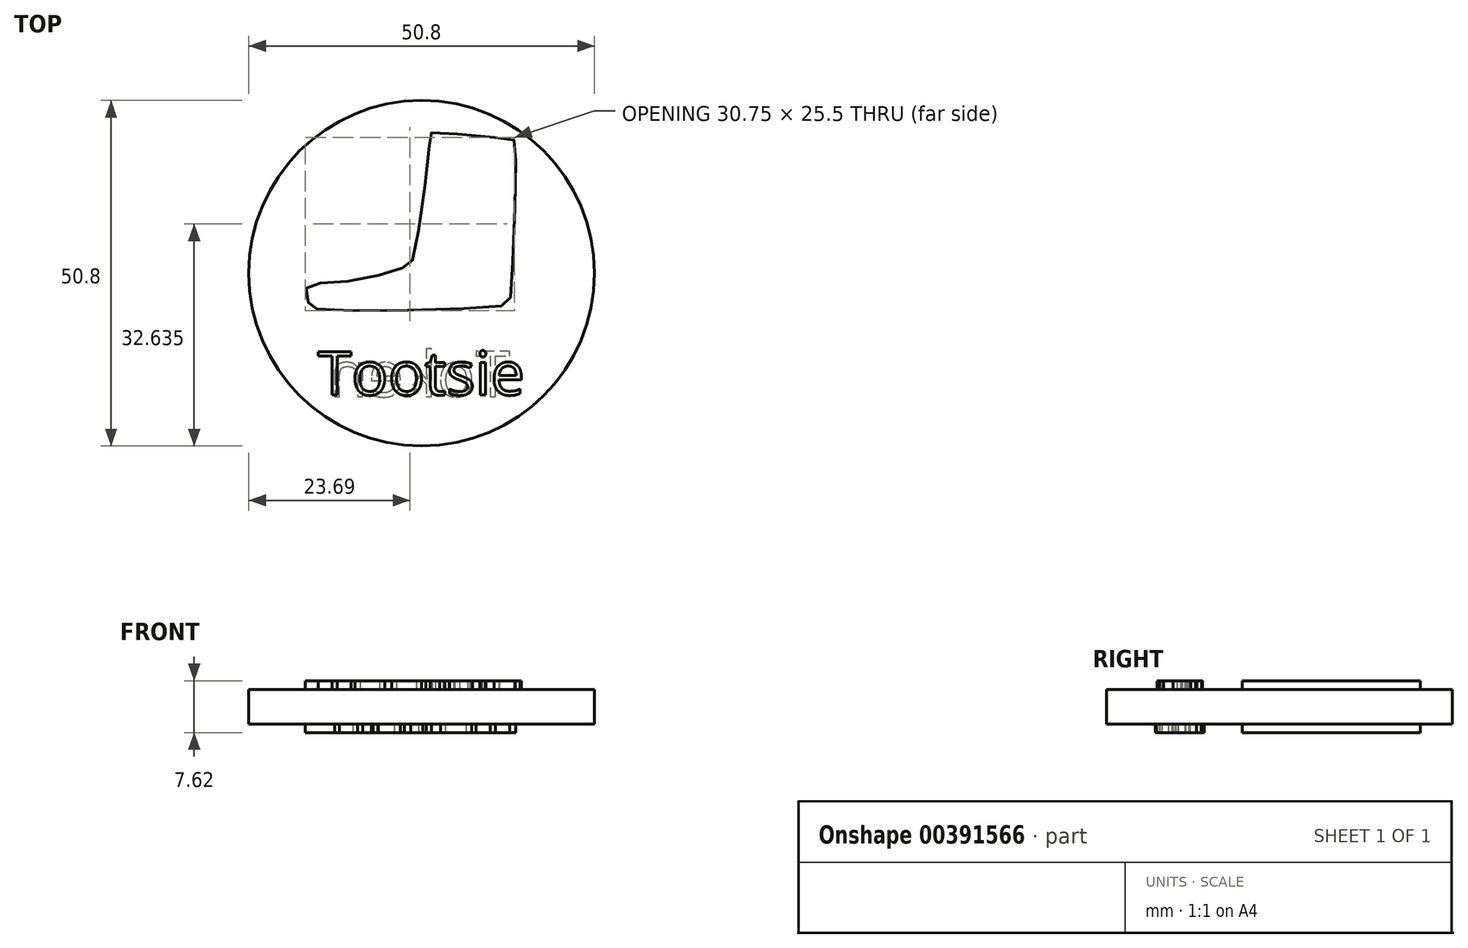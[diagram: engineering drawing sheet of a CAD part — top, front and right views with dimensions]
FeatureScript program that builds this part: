
annotation { "Feature Type Name" : "Feature", "Feature Type Description" : "" }
export const myFeature = defineFeature(function(context is Context, id is Id, definition is map)
    precondition{}
    {
        {
            var Q0;
            Q0=qCreatedBy(makeId("Top.planeOp"),FACE);
            var sketch = newSketch(context, id + "F0", { "sketchPlane" : qUnion([Q0])});
            skCircle(sketch, "E0", {"center": v(0, 0) * mm, "radius": 25.4 * mm});
            skText(sketch, "E1", { "text": "Tootsie", "fontName": "OpenSans-Regular.ttf"});
            skFitSpline(sketch, "E2", {"points": [v(11.72, -4.8) * mm, v(-15.1, -5.31) * mm, v(-16.6, -4.47) * mm, v(-16.95, -2.1) * mm, v(-11.72, -1.26) * mm, v(-2.52, 0.88) * mm, v(-1.16, 2.48) * mm, v(1.2, 20.03) * mm, v(1.54, 20.68) * mm, v(12.92, 19.73) * mm, v(13.72, 19.12) * mm, v(13.07, -3.28) * mm, v(11.72, -4.8) * mm]});
            const initialGuessF0  = {"E1": [-0.01524, -0.0179, 1, 0, 0.00642]};
            skSetInitialGuess(sketch, initialGuessF0);
            skSolve(sketch);
        }
        {
            var Q0;
            Q0=qCreatedBy(makeId("Top.planeOp"),FACE);
            var sketch = newSketch(context, id + "F1", { "sketchPlane" : qUnion([Q0])});
            skCircle(sketch, "E3", {"center": v(0, 0) * mm, "radius": 25.4 * mm});
            skSolve(sketch);
        }
        {
            var Q0;
            Q0 = qSketchRegion(id + "F1", true);
            var Q1;
            Q1 = qSketchRegion(id + "F0", true);
            extrude(context, id + "F2", {"entities" : qUnion([Q0, Q1]), "oppositeDirection" : true, "depth" : 5.08 * mm});
        }
        {
            var Q0;
            Q0=makeQuery(id+"F0.imprint","IMPRINT",FACE,{"disambiguationData":[TD([[makeQuery(id+"F0.imprint","IMPRINT",EDGE,{"derivedFrom":sQuery(id+"F0.wireOp",EDGE,"E2")}),-1.0]])]});
            extrude(context, id + "F3", {"entities" : qUnion([Q0]), "operationType" : NewBodyOperationType.ADD, "depth" : 1.27 * mm, "hasSecondDirection" : true, "secondDirectionOppositeDirection" : true, "secondDirectionDepth" : 6.35 * mm});
        }
        {
            var Q0;
            Q0=makeQuery(id+"F3.boolean.opBoolean","MERGE",FACE,{"derivedFrom":[makeQuery(id+"F2.opExtrude","CAP_FACE",FACE,{"disambiguationData":[OSD([sQuery(id+"F0.wireOp",EDGE,"E0"),sQuery(id+"F0.wireOp",EDGE,"E1.sketch_text.stroke-0"),sQuery(id+"F0.wireOp",EDGE,"E1.sketch_text.stroke-1"),sQuery(id+"F0.wireOp",EDGE,"E1.sketch_text.stroke-2"),sQuery(id+"F0.wireOp",EDGE,"E1.sketch_text.stroke-3"),sQuery(id+"F0.wireOp",EDGE,"E1.sketch_text.stroke-4"),sQuery(id+"F0.wireOp",EDGE,"E1.sketch_text.stroke-5"),sQuery(id+"F0.wireOp",EDGE,"E1.sketch_text.stroke-6"),sQuery(id+"F0.wireOp",EDGE,"E1.sketch_text.stroke-7"),sQuery(id+"F0.wireOp",EDGE,"E1.sketch_text.stroke-8"),sQuery(id+"F0.wireOp",EDGE,"E1.sketch_text.stroke-9"),sQuery(id+"F0.wireOp",EDGE,"E1.sketch_text.stroke-10"),sQuery(id+"F0.wireOp",EDGE,"E1.sketch_text.stroke-11"),sQuery(id+"F0.wireOp",EDGE,"E1.sketch_text.stroke-12"),sQuery(id+"F0.wireOp",EDGE,"E1.sketch_text.stroke-13"),sQuery(id+"F0.wireOp",EDGE,"E1.sketch_text.stroke-14"),sQuery(id+"F0.wireOp",EDGE,"E1.sketch_text.stroke-15"),sQuery(id+"F0.wireOp",EDGE,"E1.sketch_text.stroke-16"),sQuery(id+"F0.wireOp",EDGE,"E1.sketch_text.stroke-25"),sQuery(id+"F0.wireOp",EDGE,"E1.sketch_text.stroke-26"),sQuery(id+"F0.wireOp",EDGE,"E1.sketch_text.stroke-27"),sQuery(id+"F0.wireOp",EDGE,"E1.sketch_text.stroke-28"),sQuery(id+"F0.wireOp",EDGE,"E1.sketch_text.stroke-29"),sQuery(id+"F0.wireOp",EDGE,"E1.sketch_text.stroke-30"),sQuery(id+"F0.wireOp",EDGE,"E1.sketch_text.stroke-31"),sQuery(id+"F0.wireOp",EDGE,"E1.sketch_text.stroke-32"),sQuery(id+"F0.wireOp",EDGE,"E1.sketch_text.stroke-33"),sQuery(id+"F0.wireOp",EDGE,"E1.sketch_text.stroke-42"),sQuery(id+"F0.wireOp",EDGE,"E1.sketch_text.stroke-43"),sQuery(id+"F0.wireOp",EDGE,"E1.sketch_text.stroke-44"),sQuery(id+"F0.wireOp",EDGE,"E1.sketch_text.stroke-45"),sQuery(id+"F0.wireOp",EDGE,"E1.sketch_text.stroke-46"),sQuery(id+"F0.wireOp",EDGE,"E1.sketch_text.stroke-47"),sQuery(id+"F0.wireOp",EDGE,"E1.sketch_text.stroke-48"),sQuery(id+"F0.wireOp",EDGE,"E1.sketch_text.stroke-49"),sQuery(id+"F0.wireOp",EDGE,"E1.sketch_text.stroke-50"),sQuery(id+"F0.wireOp",EDGE,"E1.sketch_text.stroke-51"),sQuery(id+"F0.wireOp",EDGE,"E1.sketch_text.stroke-52"),sQuery(id+"F0.wireOp",EDGE,"E1.sketch_text.stroke-53"),sQuery(id+"F0.wireOp",EDGE,"E1.sketch_text.stroke-54"),sQuery(id+"F0.wireOp",EDGE,"E1.sketch_text.stroke-55"),sQuery(id+"F0.wireOp",EDGE,"E1.sketch_text.stroke-56"),sQuery(id+"F0.wireOp",EDGE,"E1.sketch_text.stroke-57"),sQuery(id+"F0.wireOp",EDGE,"E1.sketch_text.stroke-58"),sQuery(id+"F0.wireOp",EDGE,"E1.sketch_text.stroke-59"),sQuery(id+"F0.wireOp",EDGE,"E1.sketch_text.stroke-60"),sQuery(id+"F0.wireOp",EDGE,"E1.sketch_text.stroke-61"),sQuery(id+"F0.wireOp",EDGE,"E1.sketch_text.stroke-62"),sQuery(id+"F0.wireOp",EDGE,"E1.sketch_text.stroke-63"),sQuery(id+"F0.wireOp",EDGE,"E1.sketch_text.stroke-64"),sQuery(id+"F0.wireOp",EDGE,"E1.sketch_text.stroke-65"),sQuery(id+"F0.wireOp",EDGE,"E1.sketch_text.stroke-66"),sQuery(id+"F0.wireOp",EDGE,"E1.sketch_text.stroke-67"),sQuery(id+"F0.wireOp",EDGE,"E1.sketch_text.stroke-68"),sQuery(id+"F0.wireOp",EDGE,"E1.sketch_text.stroke-69"),sQuery(id+"F0.wireOp",EDGE,"E1.sketch_text.stroke-70"),sQuery(id+"F0.wireOp",EDGE,"E1.sketch_text.stroke-71"),sQuery(id+"F0.wireOp",EDGE,"E1.sketch_text.stroke-72"),sQuery(id+"F0.wireOp",EDGE,"E1.sketch_text.stroke-73"),sQuery(id+"F0.wireOp",EDGE,"E1.sketch_text.stroke-74"),sQuery(id+"F0.wireOp",EDGE,"E1.sketch_text.stroke-75"),sQuery(id+"F0.wireOp",EDGE,"E1.sketch_text.stroke-76"),sQuery(id+"F0.wireOp",EDGE,"E1.sketch_text.stroke-77"),sQuery(id+"F0.wireOp",EDGE,"E1.sketch_text.stroke-78"),sQuery(id+"F0.wireOp",EDGE,"E1.sketch_text.stroke-79"),sQuery(id+"F0.wireOp",EDGE,"E1.sketch_text.stroke-80"),sQuery(id+"F0.wireOp",EDGE,"E1.sketch_text.stroke-81"),sQuery(id+"F0.wireOp",EDGE,"E1.sketch_text.stroke-82"),sQuery(id+"F0.wireOp",EDGE,"E1.sketch_text.stroke-83"),sQuery(id+"F0.wireOp",EDGE,"E1.sketch_text.stroke-84"),sQuery(id+"F0.wireOp",EDGE,"E1.sketch_text.stroke-85"),sQuery(id+"F0.wireOp",EDGE,"E1.sketch_text.stroke-86"),sQuery(id+"F0.wireOp",EDGE,"E1.sketch_text.stroke-87"),sQuery(id+"F0.wireOp",EDGE,"E1.sketch_text.stroke-88"),sQuery(id+"F0.wireOp",EDGE,"E1.sketch_text.stroke-89"),sQuery(id+"F0.wireOp",EDGE,"E1.sketch_text.stroke-90"),sQuery(id+"F0.wireOp",EDGE,"E1.sketch_text.stroke-91"),sQuery(id+"F0.wireOp",EDGE,"E1.sketch_text.stroke-92"),sQuery(id+"F0.wireOp",EDGE,"E1.sketch_text.stroke-93"),sQuery(id+"F0.wireOp",EDGE,"E1.sketch_text.stroke-94"),sQuery(id+"F0.wireOp",EDGE,"E1.sketch_text.stroke-95"),sQuery(id+"F0.wireOp",EDGE,"E1.sketch_text.stroke-96"),sQuery(id+"F0.wireOp",EDGE,"E1.sketch_text.stroke-97"),sQuery(id+"F0.wireOp",EDGE,"E1.sketch_text.stroke-98"),sQuery(id+"F0.wireOp",EDGE,"E1.sketch_text.stroke-99"),sQuery(id+"F0.wireOp",EDGE,"E1.sketch_text.stroke-100"),sQuery(id+"F0.wireOp",EDGE,"E1.sketch_text.stroke-101"),sQuery(id+"F0.wireOp",EDGE,"E1.sketch_text.stroke-102"),sQuery(id+"F0.wireOp",EDGE,"E1.sketch_text.stroke-103"),sQuery(id+"F0.wireOp",EDGE,"E1.sketch_text.stroke-104"),sQuery(id+"F0.wireOp",EDGE,"E1.sketch_text.stroke-105"),sQuery(id+"F0.wireOp",EDGE,"E1.sketch_text.stroke-106"),sQuery(id+"F0.wireOp",EDGE,"E1.sketch_text.stroke-107"),sQuery(id+"F0.wireOp",EDGE,"E1.sketch_text.stroke-108"),sQuery(id+"F0.wireOp",EDGE,"E1.sketch_text.stroke-109"),sQuery(id+"F0.wireOp",EDGE,"E1.sketch_text.stroke-110"),sQuery(id+"F0.wireOp",EDGE,"E1.sketch_text.stroke-111"),sQuery(id+"F0.wireOp",EDGE,"E2")])],"isStart":false}),makeQuery(id+"F2.opExtrude","CAP_FACE",FACE,{"disambiguationData":[OSD([sQuery(id+"F1.wireOp",EDGE,"E3")])],"isStart":false})]});
            var sketch = newSketch(context, id + "F4", { "sketchPlane" : qUnion([Q0])});
            skText(sketch, "E4", { "text": "Token", "fontName": "OpenSans-Regular.ttf"});
            const initialGuessF4  = {"E4": [0.01303, 0.01815, -1, 0, 0.0067]};
            skSetInitialGuess(sketch, initialGuessF4);
            skSolve(sketch);
        }
        {
            var Q0;
            Q0=makeQuery(id+"F4.imprint","IMPRINT",FACE,{"disambiguationData":[TD([[makeQuery(id+"F4.imprint","IMPRINT",EDGE,{"derivedFrom":sQuery(id+"F4.wireOp",EDGE,"E4.sketch_text.stroke-0")}),-1.0]])]});
            var Q1;
            Q1=makeQuery(id+"F4.imprint","IMPRINT",FACE,{"disambiguationData":[TD([[makeQuery(id+"F4.imprint","IMPRINT",EDGE,{"derivedFrom":sQuery(id+"F4.wireOp",EDGE,"E4.sketch_text.stroke-8")}),-1.0]])]});
            var Q2;
            Q2=makeQuery(id+"F4.imprint","IMPRINT",FACE,{"disambiguationData":[TD([[makeQuery(id+"F4.imprint","IMPRINT",EDGE,{"derivedFrom":sQuery(id+"F4.wireOp",EDGE,"E4.sketch_text.stroke-25")}),-1.0]])]});
            var Q3;
            Q3=makeQuery(id+"F4.imprint","IMPRINT",FACE,{"disambiguationData":[TD([[makeQuery(id+"F4.imprint","IMPRINT",EDGE,{"derivedFrom":sQuery(id+"F4.wireOp",EDGE,"E4.sketch_text.stroke-40")}),-1.0]])]});
            var Q4;
            Q4=makeQuery(id+"F4.imprint","IMPRINT",FACE,{"disambiguationData":[TD([[makeQuery(id+"F4.imprint","IMPRINT",EDGE,{"derivedFrom":sQuery(id+"F4.wireOp",EDGE,"E4.sketch_text.stroke-59")}),-1.0]])]});
            extrude(context, id + "F5", {"entities" : qUnion([Q0, Q1, Q2, Q3, Q4]), "operationType" : NewBodyOperationType.ADD, "depth" : 1.27 * mm});
        }
        {
            var Q0;
            Q0=makeQuery(id+"F0.imprint","IMPRINT",FACE,{"disambiguationData":[TD([[makeQuery(id+"F0.imprint","IMPRINT",EDGE,{"derivedFrom":sQuery(id+"F0.wireOp",EDGE,"E1.sketch_text.stroke-98")}),-1.0]])]});
            var Q1;
            Q1=makeQuery(id+"F0.imprint","IMPRINT",FACE,{"disambiguationData":[TD([[makeQuery(id+"F0.imprint","IMPRINT",EDGE,{"derivedFrom":sQuery(id+"F0.wireOp",EDGE,"E1.sketch_text.stroke-86")}),-1.0]])]});
            var Q2;
            Q2=makeQuery(id+"F0.imprint","IMPRINT",FACE,{"disambiguationData":[TD([[makeQuery(id+"F0.imprint","IMPRINT",EDGE,{"derivedFrom":sQuery(id+"F0.wireOp",EDGE,"E1.sketch_text.stroke-90")}),-1.0]])]});
            var Q3;
            Q3=makeQuery(id+"F0.imprint","IMPRINT",FACE,{"disambiguationData":[TD([[makeQuery(id+"F0.imprint","IMPRINT",EDGE,{"derivedFrom":sQuery(id+"F0.wireOp",EDGE,"E1.sketch_text.stroke-61")}),-1.0]])]});
            var Q4;
            Q4=makeQuery(id+"F0.imprint","IMPRINT",FACE,{"disambiguationData":[TD([[makeQuery(id+"F0.imprint","IMPRINT",EDGE,{"derivedFrom":sQuery(id+"F0.wireOp",EDGE,"E1.sketch_text.stroke-42")}),-1.0]])]});
            var Q5;
            Q5=makeQuery(id+"F0.imprint","IMPRINT",FACE,{"disambiguationData":[TD([[makeQuery(id+"F0.imprint","IMPRINT",EDGE,{"derivedFrom":sQuery(id+"F0.wireOp",EDGE,"E1.sketch_text.stroke-25")}),-1.0]])]});
            var Q6;
            Q6=makeQuery(id+"F0.imprint","IMPRINT",FACE,{"disambiguationData":[TD([[makeQuery(id+"F0.imprint","IMPRINT",EDGE,{"derivedFrom":sQuery(id+"F0.wireOp",EDGE,"E1.sketch_text.stroke-8")}),-1.0]])]});
            var Q7;
            Q7=makeQuery(id+"F0.imprint","IMPRINT",FACE,{"disambiguationData":[TD([[makeQuery(id+"F0.imprint","IMPRINT",EDGE,{"derivedFrom":sQuery(id+"F0.wireOp",EDGE,"E1.sketch_text.stroke-0")}),-1.0]])]});
            extrude(context, id + "F6", {"entities" : qUnion([Q0, Q1, Q2, Q3, Q4, Q5, Q6, Q7]), "operationType" : NewBodyOperationType.ADD, "depth" : 1.27 * mm});
        }
    });
